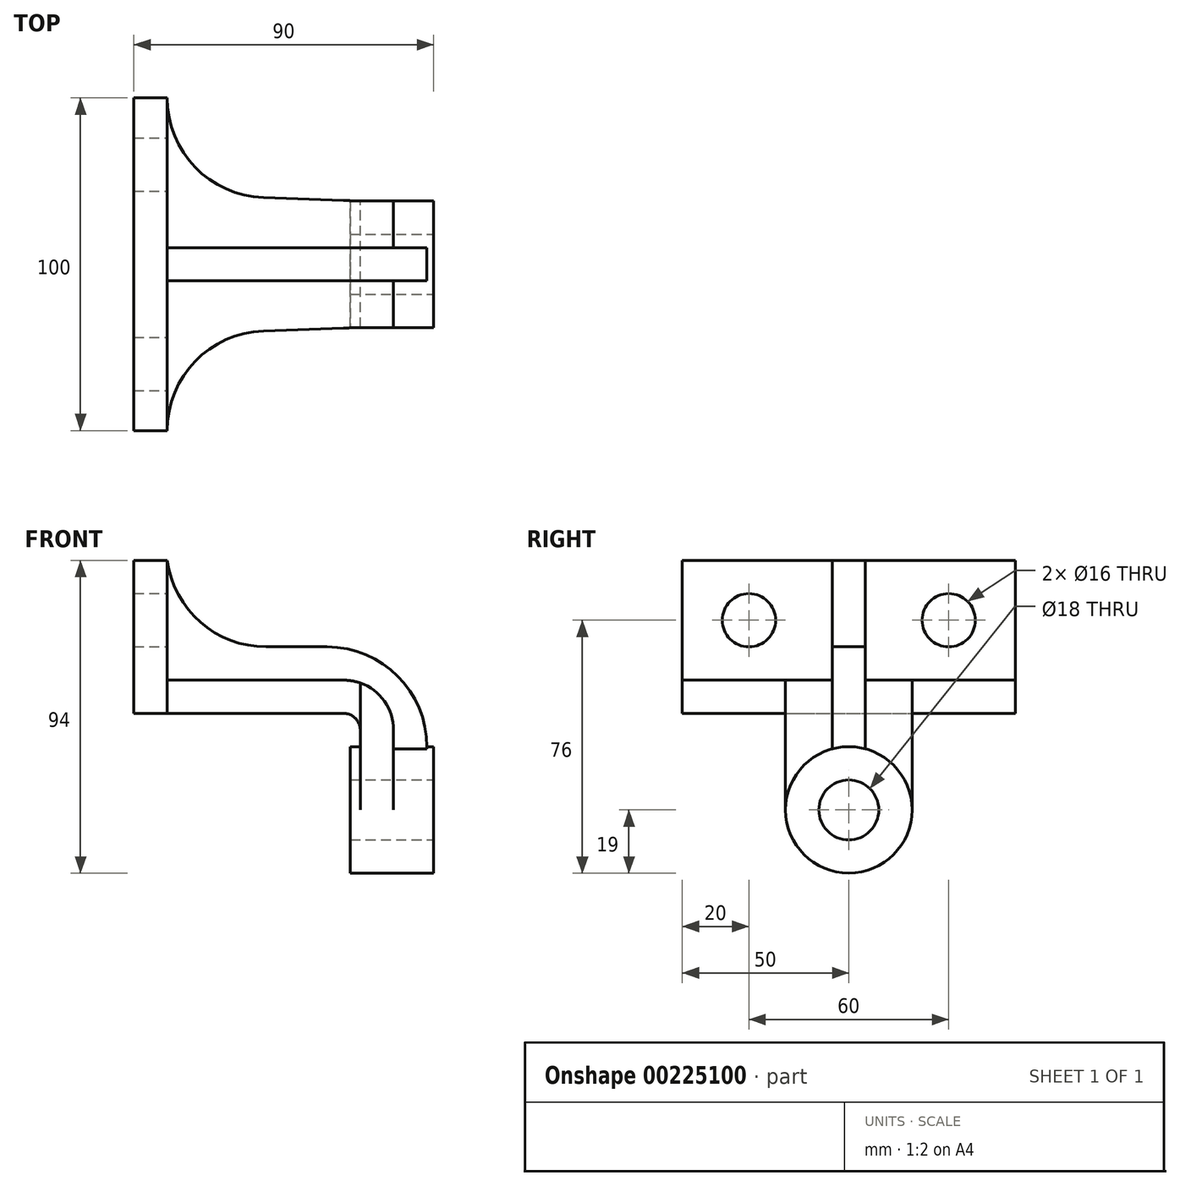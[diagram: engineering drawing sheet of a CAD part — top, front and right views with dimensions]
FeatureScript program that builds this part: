
annotation { "Feature Type Name" : "Feature", "Feature Type Description" : "" }
export const myFeature = defineFeature(function(context is Context, id is Id, definition is map)
    precondition{}
    {
        {
            var Q0;
            Q0=qCreatedBy(makeId("Front.planeOp"),FACE);
            var sketch = newSketch(context, id + "F0", { "sketchPlane" : qUnion([Q0])});
            skLineSegment(sketch, "E0", {"start": v(0, 0) * mm, "end": v(0, 46) * mm});
            skLineSegment(sketch, "E1", {"start": v(0, 46) * mm, "end": v(10, 46) * mm});
            skLineSegment(sketch, "E2", {"start": v(10, 46) * mm, "end": v(10, 10) * mm});
            skLineSegment(sketch, "E3", {"start": v(10, 10) * mm, "end": v(78, 10) * mm});
            skLineSegment(sketch, "E4", {"start": v(78, 10) * mm, "end": v(78, -29) * mm});
            skLineSegment(sketch, "E5", {"start": v(78, -29) * mm, "end": v(68, -29) * mm});
            skLineSegment(sketch, "E6", {"start": v(68, -29) * mm, "end": v(68, 10) * mm});
            skLineSegment(sketch, "E7", {"start": v(0, 0) * mm, "end": v(68, 0) * mm});
            skSolve(sketch);
        }
        {
            var Q0;
            Q0=makeQuery(id+"F0.imprint","IMPRINT",FACE,{"disambiguationData":[TD([[makeQuery(id+"F0.imprint","IMPRINT",EDGE,{"derivedFrom":sQuery(id+"F0.wireOp",EDGE,"E0")}),-1.0]])]});
            extrude(context, id + "F1", {"entities" : qUnion([Q0]), "endBound" : BoundingType.SYMMETRIC, "depth" : 100 * mm});
        }
        {
            var Q0;
            Q0 = qSketchRegion(id + "F0", true);
            extrude(context, id + "F2", {"entities" : qUnion([Q0]), "operationType" : NewBodyOperationType.ADD, "endBound" : BoundingType.SYMMETRIC, "depth" : 38 * mm});
        }
        {
            var Q0;
            {var subQ0=sQuery(id+"F0.wireOp",EDGE,"E3");Q0=makeQuery(id+"F2.boolean.opBoolean","MERGE",FACE,{"derivedFrom":[makeQuery(id+"F1.opExtrude","SWEPT_FACE",FACE,{"disambiguationData":[OSD([subQ0])]}),makeQuery(id+"F2.opExtrude","SWEPT_FACE",FACE,{"disambiguationData":[OSD([subQ0])]})]});}
            var sketch = newSketch(context, id + "F3", { "sketchPlane" : qUnion([Q0])});
            skArc(sketch, "E8", {"start": v(10, 50) * mm, "mid": v(18.42, 29.16) * mm, "end": v(38.95, 20.02) * mm});
            skArc(sketch, "E9", {"start": v(38.95, -20.02) * mm, "mid": v(18.42, -29.16) * mm, "end": v(10, -50) * mm});
            skLineSegment(sketch, "E10", {"start": v(68, 19) * mm, "end": v(38.95, 20.02) * mm});
            skLineSegment(sketch, "E11", {"start": v(68, -19) * mm, "end": v(38.95, -20.02) * mm});
            skLineSegment(sketch, "E12.0", {"start": v(10, 50) * mm, "end": v(68, 50) * mm});
            skLineSegment(sketch, "E13.0", {"start": v(68, 19) * mm, "end": v(68, 50) * mm});
            skLineSegment(sketch, "E14.0", {"start": v(10, -50) * mm, "end": v(68, -50) * mm});
            skLineSegment(sketch, "E15.0", {"start": v(10, -50) * mm, "end": v(10, 50) * mm});
            skLineSegment(sketch, "E16.0.1", {"start": v(10, 50) * mm, "end": v(0, 50) * mm});
            skLineSegment(sketch, "E16.0.2", {"start": v(0, 50) * mm, "end": v(0, -50) * mm});
            skLineSegment(sketch, "E16.0.3", {"start": v(0, -50) * mm, "end": v(10, -50) * mm});
            skLineSegment(sketch, "E17.0", {"start": v(68, -50) * mm, "end": v(68, -19) * mm});
            skSolve(sketch);
        }
        {
            var Q0;
            Q0=makeQuery(id+"F3.imprint","IMPRINT",FACE,{"disambiguationData":[TD([[makeQuery(id+"F3.imprint","IMPRINT",EDGE,{"derivedFrom":sQuery(id+"F3.wireOp",EDGE,"E9")}),1.0]])]});
            var Q1;
            Q1=makeQuery(id+"F3.imprint","IMPRINT",FACE,{"disambiguationData":[TD([[makeQuery(id+"F3.imprint","IMPRINT",EDGE,{"derivedFrom":sQuery(id+"F3.wireOp",EDGE,"E8")}),1.0]])]});
            extrude(context, id + "F4", {"entities" : qUnion([Q0, Q1]), "operationType" : NewBodyOperationType.REMOVE, "endBound" : BoundingType.UP_TO_NEXT, "oppositeDirection" : true, "depth" : 25 * mm});
        }
        {
            var Q0;
            {var subQ0=sQuery(id+"F0.wireOp",EDGE,"E7");var subQ1=sQuery(id+"F0.wireOp",EDGE,"E6");Q0=makeQuery(id+"F2.boolean.opBoolean","MERGE",EDGE,{"derivedFrom":[makeQuery(id+"F1.opExtrude","SWEPT_EDGE",EDGE,{"disambiguationData":[OSD([subQ1,subQ0])]}),makeQuery(id+"F2.opExtrude","SWEPT_EDGE",EDGE,{"disambiguationData":[OSD([subQ1,subQ0])]})]});}
            fillet(context, id + "F5", {"entities" : qUnion([Q0]), "radius" : 5 * mm, "tangentPropagation" : true, "allowEdgeOverflow" : false});
        }
        {
            var Q0;
            Q0=makeQuery(id+"F1.opExtrude","SWEPT_FACE",FACE,{"disambiguationData":[OSD([sQuery(id+"F0.wireOp",EDGE,"E2")])]});
            var sketch = newSketch(context, id + "F6", { "sketchPlane" : qUnion([Q0])});
            skLineSegment(sketch, "E18.0", {"start": v(-50, 46) * mm, "end": v(50, 46) * mm});
            skLineSegment(sketch, "E19.0", {"start": v(-50, 46) * mm, "end": v(-50, 10) * mm});
            skLineSegment(sketch, "E20.0", {"start": v(50, 46) * mm, "end": v(50, 10) * mm});
            skPoint(sketch, "E21.0", {"position": v(29.16, 10) * mm});
            skLineSegment(sketch, "E22.0", {"start": v(50, 10) * mm, "end": v(20.02, 10) * mm});
            skLineSegment(sketch, "E23.0", {"start": v(-20.02, 10) * mm, "end": v(-50, 10) * mm});
            skLineSegment(sketch, "E24.0", {"start": v(-19, 10) * mm, "end": v(19, 10) * mm});
            skLineSegment(sketch, "E25.0", {"start": v(-19, 5) * mm, "end": v(-19, -29) * mm});
            skLineSegment(sketch, "E26.0", {"start": v(19, 5) * mm, "end": v(-19, 5) * mm});
            skLineSegment(sketch, "E27.0", {"start": v(19, 5) * mm, "end": v(19, -29) * mm});
            skLineSegment(sketch, "E28.0", {"start": v(-19, -29) * mm, "end": v(19, -29) * mm});
            skCircle(sketch, "E29", {"center": v(-30, 28) * mm, "radius": 8 * mm});
            skCircle(sketch, "E30", {"center": v(30, 28) * mm, "radius": 8 * mm});
            skSolve(sketch);
        }
        {
            var Q0;
            Q0=makeQuery(id+"F6.imprint","IMPRINT",FACE,{"disambiguationData":[TD([[makeQuery(id+"F6.imprint","IMPRINT",EDGE,{"derivedFrom":sQuery(id+"F6.wireOp",EDGE,"E29")}),1.0]])]});
            var Q1;
            Q1=makeQuery(id+"F6.imprint","IMPRINT",FACE,{"disambiguationData":[TD([[makeQuery(id+"F6.imprint","IMPRINT",EDGE,{"derivedFrom":sQuery(id+"F6.wireOp",EDGE,"E30")}),1.0]])]});
            extrude(context, id + "F7", {"entities" : qUnion([Q0, Q1]), "operationType" : NewBodyOperationType.REMOVE, "oppositeDirection" : true, "depth" : 10 * mm});
        }
        {
            var Q0;
            Q0=qCreatedBy(makeId("Right.planeOp"),FACE);
            cPlane(context, id + "F8", {"entities" : qUnion([Q0]), "cplaneType" : CPlaneType.OFFSET, "offset" : 90 * mm, "width" : 150 * mm, "height" : 150 * mm});
        }
        {
            var Q0;
            Q0=qCreatedBy(id+"F8.planeOp",FACE);
            var sketch = newSketch(context, id + "F9", { "sketchPlane" : qUnion([Q0])});
            skCircle(sketch, "E31", {"center": v(0, -29) * mm, "radius": 9 * mm});
            skCircle(sketch, "E32", {"center": v(0, -29) * mm, "radius": 19 * mm});
            skSolve(sketch);
        }
        {
            var Q0;
            Q0=makeQuery(id+"F9.imprint","IMPRINT",FACE,{"disambiguationData":[TD([[makeQuery(id+"F9.imprint","IMPRINT",EDGE,{"derivedFrom":sQuery(id+"F9.wireOp",EDGE,"E31")}),-1.0]])]});
            extrude(context, id + "F10", {"entities" : qUnion([Q0]), "operationType" : NewBodyOperationType.ADD, "oppositeDirection" : true, "depth" : 25 * mm});
        }
        {
            var Q0;
            Q0=makeQuery(id+"F10.boolean.opBoolean","SPLIT",FACE,{"disambiguationData":[TD([makeQuery(id+"F2.opExtrude","SWEPT_FACE",FACE,{"disambiguationData":[OSD([sQuery(id+"F0.wireOp",EDGE,"E5")])]})])],"derivedFrom":makeQuery(id+"F2.opExtrude","SWEPT_FACE",FACE,{"disambiguationData":[OSD([sQuery(id+"F0.wireOp",EDGE,"E4")])]})});
            extrude(context, id + "F11", {"entities" : qUnion([Q0]), "operationType" : NewBodyOperationType.REMOVE, "oppositeDirection" : true, "depth" : 25 * mm});
        }
        {
            var Q0;
            Q0=qCreatedBy(makeId("Front.planeOp"),FACE);
            var sketch = newSketch(context, id + "F12", { "sketchPlane" : qUnion([Q0])});
            skLineSegment(sketch, "E33.0", {"start": v(10, 46) * mm, "end": v(10, 10) * mm});
            skLineSegment(sketch, "E34.0", {"start": v(38.95, 10) * mm, "end": v(10, 10) * mm});
            skLineSegment(sketch, "E35.0", {"start": v(68, 10) * mm, "end": v(38.95, 10) * mm});
            skArc(sketch, "E36", {"start": v(10, 46) * mm, "mid": v(19.98, 27.42) * mm, "end": v(39.73, 20) * mm});
            skPoint(sketch, "E37.endSnap0", {"position": v(48.87, 20) * mm});
            skLineSegment(sketch, "E38", {"start": v(65, -10) * mm, "end": v(68, -10) * mm, "construction": true});
            skLineSegment(sketch, "E39", {"start": v(65, -10) * mm, "end": v(90, -10) * mm});
            skArc(sketch, "E40.trimOffspring", {"start": v(88, -10) * mm, "mid": v(79.21, 11.21) * mm, "end": v(58, 20) * mm});
            skLineSegment(sketch, "E41.0", {"start": v(78, 5) * mm, "end": v(78, -29) * mm});
            skPoint(sketch, "E42.0", {"position": v(76.54, 8.54) * mm});
            skLineSegment(sketch, "E43.0.0", {"start": v(78, -29) * mm, "end": v(78, 5) * mm});
            skArc(sketch, "E43.0.1", {"start": v(78, 5) * mm, "mid": v(76.54, 8.54) * mm, "end": v(73, 10) * mm});
            skLineSegment(sketch, "E43.0.2", {"start": v(73, 10) * mm, "end": v(68, 10) * mm});
            skLineSegment(sketch, "E43.0.3", {"start": v(68, 10) * mm, "end": v(68, -5) * mm});
            skLineSegment(sketch, "E43.0.4", {"start": v(68, -5) * mm, "end": v(68, -29) * mm});
            skLineSegment(sketch, "E43.0.5", {"start": v(68, -29) * mm, "end": v(78, -29) * mm});
            skPoint(sketch, "E44.orphan", {"position": v(134.55, 20) * mm});
            skLineSegment(sketch, "E45", {"start": v(39.73, 20) * mm, "end": v(58, 20) * mm});
            skLineSegment(sketch, "E46", {"start": v(88, -10) * mm, "end": v(88, -29) * mm});
            skLineSegment(sketch, "E47.trimOffspring", {"start": v(78, -10) * mm, "end": v(90, -10) * mm, "construction": true});
            skLineSegment(sketch, "E48", {"start": v(88, -29) * mm, "end": v(78, -29) * mm});
            skLineSegment(sketch, "E49", {"start": v(78, -29) * mm, "end": v(78, -10) * mm});
            skSolve(sketch);
        }
        {
            var Q0;
            Q0 = qSketchRegion(id + "F12", true);
            extrude(context, id + "F13", {"entities" : qUnion([Q0]), "operationType" : NewBodyOperationType.ADD, "endBound" : BoundingType.SYMMETRIC, "depth" : 10 * mm});
        }
        {
            var Q0;
            {var subQ0=sQuery(id+"F12.wireOp",EDGE,"E48");var subQ1=sQuery(id+"F12.wireOp",EDGE,"E46");var subQ2=sQuery(id+"F12.wireOp",EDGE,"E45");var subQ3=sQuery(id+"F12.wireOp",EDGE,"E43.0.5");var subQ4=sQuery(id+"F12.wireOp",EDGE,"E43.0.4");var subQ5=sQuery(id+"F12.wireOp",EDGE,"E43.0.3");var subQ6=sQuery(id+"F12.wireOp",EDGE,"E40.trimOffspring");var subQ7=sQuery(id+"F12.wireOp",EDGE,"E36");var subQ8=sQuery(id+"F12.wireOp",EDGE,"E35.0");var subQ9=sQuery(id+"F12.wireOp",EDGE,"E34.0");var subQ10=sQuery(id+"F12.wireOp",EDGE,"E33.0");var subQ11=sQuery(id+"F9.wireOp",EDGE,"E31");Q0=makeQuery(id+"F13.boolean.opBoolean","SPLIT",FACE,{"disambiguationData":[TD([makeQuery(id+"F10.opExtrude","SWEPT_FACE",FACE,{"disambiguationData":[OSD([subQ11])]}),makeQuery(id+"F11.opExtrude","SWEPT_FACE",FACE,{"disambiguationData":[OSD([sQuery(id+"F0.wireOp",EDGE,"E4"),subQ11])]}),makeQuery(id+"F13.opExtrude","CAP_FACE",FACE,{"disambiguationData":[OSD([subQ10,subQ9,subQ8,subQ7,subQ6,subQ5,subQ4,subQ3,subQ2,subQ1,subQ0])],"isStart":true}),makeQuery(id+"F13.opExtrude","CAP_FACE",FACE,{"disambiguationData":[OSD([subQ10,subQ9,subQ8,subQ7,subQ6,subQ5,subQ4,subQ3,subQ2,subQ1,subQ0])],"isStart":false}),makeQuery(id+"F13.opExtrude","SWEPT_FACE",FACE,{"disambiguationData":[OSD([subQ3,subQ0])]})])],"derivedFrom":makeQuery(id+"F13.opExtrude","SWEPT_FACE",FACE,{"disambiguationData":[OSD([subQ1])]})});}
            extrude(context, id + "F14", {"entities" : qUnion([Q0]), "operationType" : NewBodyOperationType.REMOVE, "oppositeDirection" : true, "depth" : 25 * mm});
        }
        {
            var Q0;
            {var subQ0=sQuery(id+"F0.wireOp",EDGE,"E4");var subQ1=sQuery(id+"F0.wireOp",EDGE,"E3");Q0=makeQuery(id+"F13.boolean.opBoolean","SPLIT",EDGE,{"disambiguationData":[TD([makeQuery(id+"F2.opExtrude","CAP_FACE",FACE,{"disambiguationData":[OSD([sQuery(id+"F0.wireOp",EDGE,"E0"),sQuery(id+"F0.wireOp",EDGE,"E1"),sQuery(id+"F0.wireOp",EDGE,"E2"),subQ1,subQ0,sQuery(id+"F0.wireOp",EDGE,"E5"),sQuery(id+"F0.wireOp",EDGE,"E6"),sQuery(id+"F0.wireOp",EDGE,"E7")])],"isStart":false})])],"derivedFrom":makeQuery(id+"F2.opExtrude","SWEPT_EDGE",EDGE,{"disambiguationData":[OSD([subQ1,subQ0])]})});}
            var Q1;
            {var subQ0=sQuery(id+"F0.wireOp",EDGE,"E4");var subQ1=sQuery(id+"F0.wireOp",EDGE,"E3");Q1=makeQuery(id+"F13.boolean.opBoolean","SPLIT",EDGE,{"disambiguationData":[TD([makeQuery(id+"F2.opExtrude","CAP_FACE",FACE,{"disambiguationData":[OSD([sQuery(id+"F0.wireOp",EDGE,"E0"),sQuery(id+"F0.wireOp",EDGE,"E1"),sQuery(id+"F0.wireOp",EDGE,"E2"),subQ1,subQ0,sQuery(id+"F0.wireOp",EDGE,"E5"),sQuery(id+"F0.wireOp",EDGE,"E6"),sQuery(id+"F0.wireOp",EDGE,"E7")])],"isStart":true})])],"derivedFrom":makeQuery(id+"F2.opExtrude","SWEPT_EDGE",EDGE,{"disambiguationData":[OSD([subQ1,subQ0])]})});}
            fillet(context, id + "F15", {"entities" : qUnion([Q0, Q1]), "radius" : 15 * mm, "tangentPropagation" : true, "allowEdgeOverflow" : false});
        }
    });
